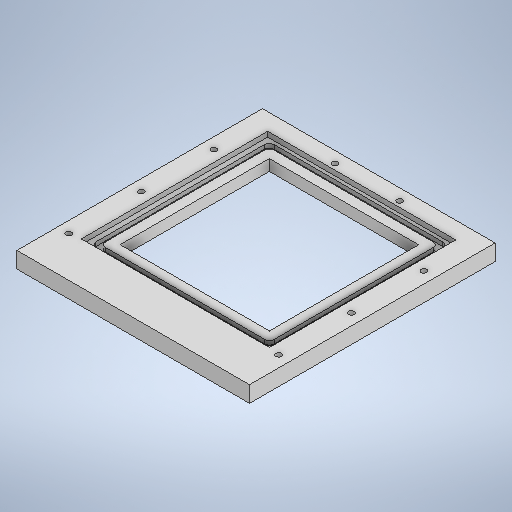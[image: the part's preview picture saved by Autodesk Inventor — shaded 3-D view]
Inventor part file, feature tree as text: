
AUTODESK INVENTOR PART (.ipt)
format: ipt  version: 2025.2 (Build 292293000, 293)  size: 369,664 bytes
history: native  units: in
note: dims shown in document units (in); Inventor stores cm internally (conversion verified against a paired STEP export)
features: extrude x5, sketch x5, hole x1
ambient origin geometry x8: Origin, YZ Plane, XZ Plane, XY Plane, X Axis, Y Axis, Z Axis, Center Point
bodies: Solid1 (feature_tree)
feature tree (11):
  extrude  "Extrusion1"  Depth=5.6693in
  extrude  "Extrusion2"  Depth=3.6369in
  hole  "Hole1"  [1 undecoded]
  sketch  "Sketch4"  dims[d14=3.6403in d15=1.0145in]
  extrude  "Extrusion3"  Depth=0.3937in TaperAngle=0.0deg
  extrude  "Extrusion4"  Depth=5.6693in
  extrude  "Extrusion5"  Depth=5.9843in
  sketch  "Sketch1"  dims[d3=5.9843in d4=5.6693in]
  sketch  "Sketch2"  dims[d5=0.3937in d6=0.0in]
  sketch  "Sketch3"  dims[d7=0.3543in d8=0.3543in d9=0.3543in d10=0.3543in d11=0.1181in d12=0.1181in d13=3.6369in]
  sketch  "Sketch5"  dims[d16=0.8478in d17=0.3937in d18=0.0in d19=5.6693in d20=5.9843in d21=1.7717in d22=1.7717in d23=1.7717in d24=1.7717in d25=0.5722in d26=0.5722in d27=1.5748in d28=2.0472in d29=0.2756in d30=0.2756in d31=0.2756in d32=0.2756in d33=0.2756in d34=0.9843in d36=0.9843in d37=0.1378in d38=0.2362in d39=0.1575in d40=0.0787in d41=90.0deg d42=0.315in d43=0.8108in d44=0.3543in d45=0.3543in d46=0.3543in d47=0.3543in d48=0.1181in d49=0.1181in d51=0.0in d52=0.0in d53=0.0in d54=0.0in d55=0.0984in d56=0.0in d58=0.1181in d59=0.1181in d60=0.1181in d61=0.122in d62=0.0in d63=0.2205in d64=0.0in d65=0.0787in]
note: 1 required parameter value undecoded (feature->parameter linkage not recoverable at this tier; creation-order binding heuristic only, values carry confidence <= 0.55)
